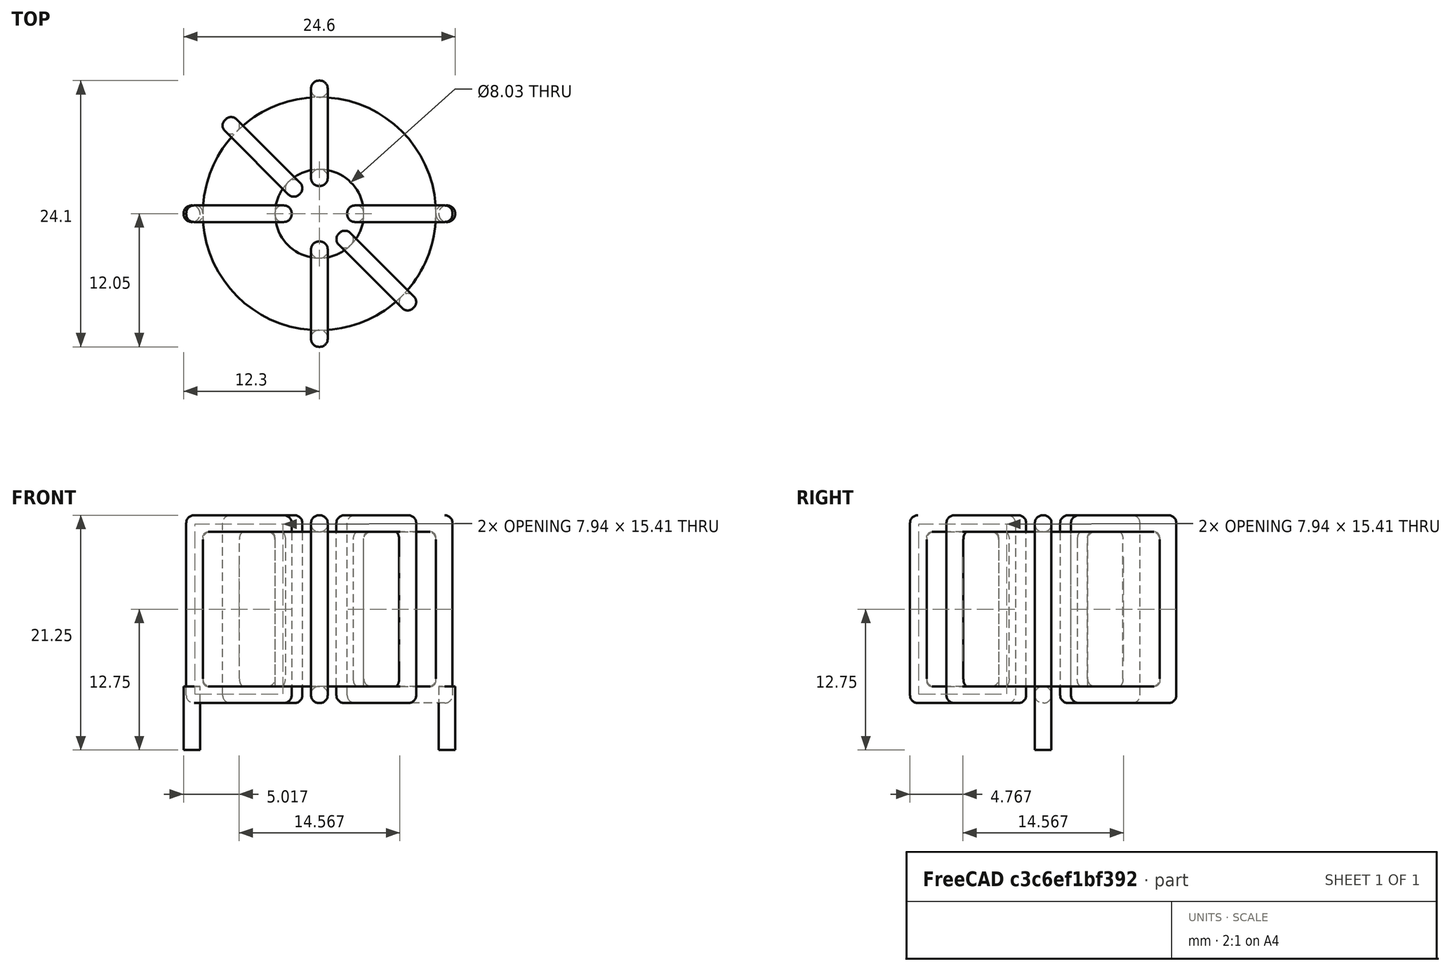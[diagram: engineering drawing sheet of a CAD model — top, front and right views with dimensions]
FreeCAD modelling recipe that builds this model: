
FCSTD DOCUMENT  (FreeCAD 0.16R6703 (Git))
Label: L_Toroid_Horizontal_D24.1mm_P23.10mm_Bourns_2200series
License: All rights reserved
LicenseURL: http://en.wikipedia.org/wiki/All_rights_reserved
objects: Sketcher::SketchObject×6, PartDesign::Pad×6, PartDesign::Fillet×5, Spreadsheet::Sheet×1
note: 23 computed .brp shape members not serialized (recipe doc carries the construction recipe); baked Part::Feature solids carry a one-line shape summary decoded from their .brp

FEATURE [Spreadsheet::Sheet] Spreadsheet  label="dimensions"
  cells = A1=Wx; B1(Wx)=24.1; C1(WW)=8.033333333333333; D1=24.1; A2=Wy; B2(Wy)=24.1; D2=24.1; A3=RM; B3(RMx)=23.1; C3(RMy)=0; A4=d_wire; B4(d_wire)=1.5; A5=H; B5(H)=14; A6=offsetx; B6(offsetx)=0.5
FEATURE [Sketcher::SketchObject] Sketch
  Placement = pos=(0,0,2) rot=(0,0,1;0rad)
  expr: Placement.Base.z = 0.5 + Spreadsheet.d_wire
  expr: Constraints[0] = Spreadsheet.Wx / 2 - Spreadsheet.d_wire
  expr: Constraints[4] = Spreadsheet.WW / 2
  expr: Constraints[2] = Spreadsheet.RMy / 2
  expr: Constraints[1] = Spreadsheet.RMx / 2
  sketch-geometry (2):
    g0: Circle CenterX=11.55 CenterY=0 CenterZ=0 NormalX=0 NormalY=0 NormalZ=1 Radius=10.55
    g1: Circle CenterX=11.55 CenterY=0 CenterZ=0 NormalX=0 NormalY=0 NormalZ=1 Radius=4.01667
  constraints (5):
    c: Radius(g0) = 10.55
    c: DistanceX(g-1,g0) = 11.55
    c: DistanceY(g-1,g0) = 0
    c: Coincident(g1,g0)
    c: Radius(g1) = 4.01667
FEATURE [PartDesign::Pad] Pad
  Length = 14
  Length2 = 100
  Placement = pos=(0,0,2) rot=(0,0,1;0rad)
  Sketch = -> Sketch
  Type = 0
  expr: Length = Spreadsheet.H
FEATURE [Sketcher::SketchObject] Sketch001
  Placement = pos=(0,0,1.25) rot=(0,0,1;0rad)
  expr: Placement.Base.z = 0.5 + Spreadsheet.d_wire * 0.5
  expr: Constraints[4] = Spreadsheet.RMx
  expr: Constraints[2] = Spreadsheet.RMy
  expr: Constraints[1] = Spreadsheet.d_wire / 2
  sketch-geometry (2):
    g0: Circle CenterX=0 CenterY=0 CenterZ=0 NormalX=0 NormalY=0 NormalZ=1 Radius=0.75
    g1: Circle CenterX=23.1 CenterY=0 CenterZ=0 NormalX=0 NormalY=0 NormalZ=1 Radius=0.75
  constraints (5):
    c: Equal(g0,g1)
    c: Radius(g0) = 0.75
    c: DistanceY(g-1,g1) = 0
    c: Coincident(g0,g-1)
    c: DistanceX(g-1,g1) = 23.1
FEATURE [PartDesign::Pad] Pad001
  Length = 0.75
  Length2 = 5
  Placement = pos=(0,0,1.25) rot=(0,0,1;0rad)
  Reversed = true
  Sketch = -> Sketch001
  Type = 4
  expr: Length2 = 3.5 + Spreadsheet.d_wire
  expr: Length = Spreadsheet.d_wire / 2
FEATURE [PartDesign::Fillet] Fillet
  Base = -> Pad [Edge6,Edge3,Edge2]
  Placement = pos=(0,0,2) rot=(0,0,1;0rad)
  Radius = 0.5
FEATURE [Sketcher::SketchObject] Sketch003
  Placement = pos=(11.55,0,0) rot=(1,0,0;1.5708rad)
  expr: Placement.Base.x = Spreadsheet.RMx / 2
  expr: Constraints[49] = Spreadsheet.Wx - Spreadsheet.d_wire * 2
  expr: Constraints[44] = Spreadsheet.d_wire
  expr: Constraints[23] = Spreadsheet.H
  expr: Constraints[22] = Spreadsheet.Wx / 2 - Spreadsheet.d_wire
  expr: Placement.Base.y = Spreadsheet.RMy / 2
  expr: Constraints[21] = (Spreadsheet.Wx - Spreadsheet.WW) / 2 - Spreadsheet.d_wire
  expr: Constraints[19] = Spreadsheet.d_wire
  expr: Constraints[17] = Spreadsheet.d_wire
  expr: Constraints[18] = Spreadsheet.d_wire
  expr: Constraints[16] = Spreadsheet.d_wire
  sketch-geometry (16):
    g0: LineSegment StartX=-2.51667 StartY=0.5 StartZ=0 EndX=-12.05 EndY=0.5 EndZ=0
    g1: LineSegment StartX=-12.05 StartY=0.5 StartZ=0 EndX=-12.05 EndY=17.5 EndZ=0
    g2: LineSegment StartX=-12.05 StartY=17.5 StartZ=0 EndX=-2.51667 EndY=17.5 EndZ=0
    g3: LineSegment StartX=-2.51667 StartY=17.5 StartZ=0 EndX=-2.51667 EndY=0.5 EndZ=0
    g4: LineSegment StartX=-10.55 StartY=16 StartZ=0 EndX=-4.01667 EndY=16 EndZ=0
    g5: LineSegment StartX=-4.01667 StartY=16 StartZ=0 EndX=-4.01667 EndY=2 EndZ=0
    g6: LineSegment StartX=-4.01667 StartY=2 StartZ=0 EndX=-10.55 EndY=2 EndZ=0
    g7: LineSegment StartX=-10.55 StartY=2 StartZ=0 EndX=-10.55 EndY=16 EndZ=0
    g8: LineSegment StartX=2.51667 StartY=17.5 StartZ=0 EndX=12.05 EndY=17.5 EndZ=0
    g9: LineSegment StartX=12.05 StartY=17.5 StartZ=0 EndX=12.05 EndY=0.5 EndZ=0
    g10: LineSegment StartX=12.05 StartY=0.5 StartZ=0 EndX=2.51667 EndY=0.5 EndZ=0
    g11: LineSegment StartX=2.51667 StartY=0.5 StartZ=0 EndX=2.51667 EndY=17.5 EndZ=0
    g12: LineSegment StartX=4.01667 StartY=16 StartZ=0 EndX=10.55 EndY=16 EndZ=0
    g13: LineSegment StartX=10.55 StartY=16 StartZ=0 EndX=10.55 EndY=2 EndZ=0
    g14: LineSegment StartX=10.55 StartY=2 StartZ=0 EndX=4.01667 EndY=2 EndZ=0
    g15: LineSegment StartX=4.01667 StartY=2 StartZ=0 EndX=4.01667 EndY=16 EndZ=0
  constraints (50):
    c: Horizontal(g0)
    c: Coincident(g1,g0)
    c: Vertical(g1)
    c: Coincident(g2,g1)
    c: Horizontal(g2)
    c: Coincident(g3,g2)
    c: Coincident(g3,g0)
    c: Vertical(g3)
    c: Coincident(g4,g5)
    c: Coincident(g5,g6)
    c: Coincident(g6,g7)
    c: Coincident(g7,g4)
    c: Horizontal(g4)
    c: Horizontal(g6)
    c: Vertical(g5)
    c: Vertical(g7)
    c: DistanceX(g1,g4) = 1.5
    c: DistanceY(g4,g1) = 1.5
    c: DistanceX(g5,g0) = 1.5
    c: DistanceY(g0,g5) = 1.5
    c: DistanceY(g-1,g0) = 0.5
    c: DistanceX(g6,g6) = 6.53333
    c: DistanceX(g6,g-1) = 10.55
    c: DistanceY(g7,g7) = 14
    c: Coincident(g8,g9)
    c: Coincident(g9,g10)
    c: Coincident(g10,g11)
    c: Coincident(g11,g8)
    c: Horizontal(g8)
    c: Horizontal(g10)
    c: Vertical(g9)
    c: Vertical(g11)
    c: Coincident(g12,g13)
    c: Coincident(g13,g14)
    c: Coincident(g14,g15)
    c: Coincident(g15,g12)
    c: Horizontal(g12)
    c: Horizontal(g14)
    c: Vertical(g13)
    c: Vertical(g15)
    c: DistanceY(g8,g2) = 0
    c: DistanceY(g10,g0) = 0
    c: DistanceY(g14,g5) = 0
    c: DistanceY(g12,g4) = 0
    c: DistanceX(g8,g12) = 1.5
    c: Equal(g8,g2)
    c: Equal(g12,g4)
    c: Equal(g9,g1)
    c: Equal(g13,g7)
    c: DistanceX(g4,g12) = 21.1
FEATURE [PartDesign::Pad] Pad002
  Length = 1.5
  Length2 = 100
  Midplane = true
  Placement = pos=(11.55,0,0) rot=(1,0,0;1.5708rad)
  Sketch = -> Sketch003
  Type = 0
  expr: Length = Spreadsheet.d_wire
FEATURE [PartDesign::Fillet] Fillet001
  Base = -> Pad002 [Edge38,Edge41,Edge42,Edge43,Edge29,Edge32,Edge33,Edge34,Edge25,Edge35,Edge36,Edge13,Edge14,Edge15,Edge16,Edge17,Edge18,Edge19,Edge1,Edge2,Edge3,Edge4,Edge5,Edge6,Edge7,Edge37,Edge39,Edge40,Edge20,Edge23,Edge24,Edge21,Edge22,Edge8,Edge9,Edge10,Edge11,Edge12,Edge26,Edge27,+8 more]
  Placement = pos=(11.55,0,0) rot=(1,0,0;1.5708rad)
  Radius = 0.705
  expr: Radius = Spreadsheet.d_wire * 0.47
FEATURE [Sketcher::SketchObject] Sketch004
  Placement = pos=(11.55,0,0) rot=(0.862856,0.357407,0.357407;1.71777rad)
  expr: Placement.Base.x = Spreadsheet.RMx / 2
  expr: Constraints[49] = Spreadsheet.Wx - 2 * Spreadsheet.d_wire
  expr: Constraints[44] = Spreadsheet.d_wire
  expr: Constraints[23] = Spreadsheet.H
  expr: Constraints[22] = Spreadsheet.Wx / 2 - Spreadsheet.d_wire
  expr: Placement.Base.y = Spreadsheet.RMy / 2
  expr: Constraints[21] = (Spreadsheet.Wx - Spreadsheet.WW) / 2 - Spreadsheet.d_wire
  expr: Constraints[19] = Spreadsheet.d_wire
  expr: Constraints[17] = Spreadsheet.d_wire
  expr: Constraints[18] = Spreadsheet.d_wire
  expr: Constraints[16] = Spreadsheet.d_wire
  sketch-geometry (16):
    g0: LineSegment StartX=-2.51667 StartY=0.5 StartZ=0 EndX=-12.05 EndY=0.5 EndZ=0
    g1: LineSegment StartX=-12.05 StartY=0.5 StartZ=0 EndX=-12.05 EndY=17.5 EndZ=0
    g2: LineSegment StartX=-12.05 StartY=17.5 StartZ=0 EndX=-2.51667 EndY=17.5 EndZ=0
    g3: LineSegment StartX=-2.51667 StartY=17.5 StartZ=0 EndX=-2.51667 EndY=0.5 EndZ=0
    g4: LineSegment StartX=-10.55 StartY=16 StartZ=0 EndX=-4.01667 EndY=16 EndZ=0
    g5: LineSegment StartX=-4.01667 StartY=16 StartZ=0 EndX=-4.01667 EndY=2 EndZ=0
    g6: LineSegment StartX=-4.01667 StartY=2 StartZ=0 EndX=-10.55 EndY=2 EndZ=0
    g7: LineSegment StartX=-10.55 StartY=2 StartZ=0 EndX=-10.55 EndY=16 EndZ=0
    g8: LineSegment StartX=2.51667 StartY=17.5 StartZ=0 EndX=12.05 EndY=17.5 EndZ=0
    g9: LineSegment StartX=12.05 StartY=17.5 StartZ=0 EndX=12.05 EndY=0.5 EndZ=0
    g10: LineSegment StartX=12.05 StartY=0.5 StartZ=0 EndX=2.51667 EndY=0.5 EndZ=0
    g11: LineSegment StartX=2.51667 StartY=0.5 StartZ=0 EndX=2.51667 EndY=17.5 EndZ=0
    g12: LineSegment StartX=4.01667 StartY=16 StartZ=0 EndX=10.55 EndY=16 EndZ=0
    g13: LineSegment StartX=10.55 StartY=16 StartZ=0 EndX=10.55 EndY=2 EndZ=0
    g14: LineSegment StartX=10.55 StartY=2 StartZ=0 EndX=4.01667 EndY=2 EndZ=0
    g15: LineSegment StartX=4.01667 StartY=2 StartZ=0 EndX=4.01667 EndY=16 EndZ=0
  constraints (50):
    c: Horizontal(g0)
    c: Coincident(g1,g0)
    c: Vertical(g1)
    c: Coincident(g2,g1)
    c: Horizontal(g2)
    c: Coincident(g3,g2)
    c: Coincident(g3,g0)
    c: Vertical(g3)
    c: Coincident(g4,g5)
    c: Coincident(g5,g6)
    c: Coincident(g6,g7)
    c: Coincident(g7,g4)
    c: Horizontal(g4)
    c: Horizontal(g6)
    c: Vertical(g5)
    c: Vertical(g7)
    c: DistanceX(g1,g4) = 1.5
    c: DistanceY(g4,g1) = 1.5
    c: DistanceX(g5,g0) = 1.5
    c: DistanceY(g0,g5) = 1.5
    c: DistanceY(g-1,g0) = 0.5
    c: DistanceX(g6,g6) = 6.53333
    c: DistanceX(g6,g-1) = 10.55
    c: DistanceY(g7,g7) = 14
    c: Coincident(g8,g9)
    c: Coincident(g9,g10)
    c: Coincident(g10,g11)
    c: Coincident(g11,g8)
    c: Horizontal(g8)
    c: Horizontal(g10)
    c: Vertical(g9)
    c: Vertical(g11)
    c: Coincident(g12,g13)
    c: Coincident(g13,g14)
    c: Coincident(g14,g15)
    c: Coincident(g15,g12)
    c: Horizontal(g12)
    c: Horizontal(g14)
    c: Vertical(g13)
    c: Vertical(g15)
    c: DistanceY(g8,g2) = 0
    c: DistanceY(g10,g0) = 0
    c: DistanceY(g14,g5) = 0
    c: DistanceY(g12,g4) = 0
    c: DistanceX(g8,g12) = 1.5
    c: Equal(g8,g2)
    c: Equal(g12,g4)
    c: Equal(g9,g1)
    c: Equal(g13,g7)
    c: DistanceX(g4,g12) = 21.1
FEATURE [PartDesign::Pad] Pad003
  Length = 1.5
  Length2 = 100
  Midplane = true
  Placement = pos=(11.55,0,0) rot=(0.862856,0.357407,0.357407;1.71777rad)
  Sketch = -> Sketch004
  Type = 0
  expr: Length = Spreadsheet.d_wire
FEATURE [PartDesign::Fillet] Fillet002
  Base = -> Pad003 [Edge38,Edge41,Edge42,Edge43,Edge29,Edge32,Edge33,Edge34,Edge25,Edge35,Edge36,Edge13,Edge14,Edge15,Edge16,Edge17,Edge18,Edge19,Edge1,Edge2,Edge3,Edge4,Edge5,Edge6,Edge7,Edge37,Edge39,Edge40,Edge20,Edge23,Edge24,Edge21,Edge22,Edge8,Edge9,Edge10,Edge11,Edge12,Edge26,Edge27,+8 more]
  Placement = pos=(11.55,0,0) rot=(0.862856,0.357407,0.357407;1.71777rad)
  Radius = 0.705
  expr: Radius = Spreadsheet.d_wire * 0.47
FEATURE [Sketcher::SketchObject] Sketch005
  Placement = pos=(11.55,0,0) rot=(0.862856,-0.357407,-0.357407;1.71777rad)
  expr: Placement.Base.x = Spreadsheet.RMx / 2
  expr: Constraints[49] = Spreadsheet.Wx - 2 * Spreadsheet.d_wire
  expr: Constraints[44] = Spreadsheet.d_wire
  expr: Constraints[23] = Spreadsheet.H
  expr: Constraints[22] = Spreadsheet.Wx / 2 - Spreadsheet.d_wire
  expr: Placement.Base.y = Spreadsheet.RMy / 2
  expr: Constraints[21] = (Spreadsheet.Wx - Spreadsheet.WW) / 2 - Spreadsheet.d_wire
  expr: Constraints[19] = Spreadsheet.d_wire
  expr: Constraints[17] = Spreadsheet.d_wire
  expr: Constraints[18] = Spreadsheet.d_wire
  expr: Constraints[16] = Spreadsheet.d_wire
  sketch-geometry (16):
    g0: LineSegment StartX=-2.51667 StartY=0.5 StartZ=0 EndX=-12.05 EndY=0.5 EndZ=0
    g1: LineSegment StartX=-12.05 StartY=0.5 StartZ=0 EndX=-12.05 EndY=17.5 EndZ=0
    g2: LineSegment StartX=-12.05 StartY=17.5 StartZ=0 EndX=-2.51667 EndY=17.5 EndZ=0
    g3: LineSegment StartX=-2.51667 StartY=17.5 StartZ=0 EndX=-2.51667 EndY=0.5 EndZ=0
    g4: LineSegment StartX=-10.55 StartY=16 StartZ=0 EndX=-4.01667 EndY=16 EndZ=0
    g5: LineSegment StartX=-4.01667 StartY=16 StartZ=0 EndX=-4.01667 EndY=2 EndZ=0
    g6: LineSegment StartX=-4.01667 StartY=2 StartZ=0 EndX=-10.55 EndY=2 EndZ=0
    g7: LineSegment StartX=-10.55 StartY=2 StartZ=0 EndX=-10.55 EndY=16 EndZ=0
    g8: LineSegment StartX=2.51667 StartY=17.5 StartZ=0 EndX=12.05 EndY=17.5 EndZ=0
    g9: LineSegment StartX=12.05 StartY=17.5 StartZ=0 EndX=12.05 EndY=0.5 EndZ=0
    g10: LineSegment StartX=12.05 StartY=0.5 StartZ=0 EndX=2.51667 EndY=0.5 EndZ=0
    g11: LineSegment StartX=2.51667 StartY=0.5 StartZ=0 EndX=2.51667 EndY=17.5 EndZ=0
    g12: LineSegment StartX=4.01667 StartY=16 StartZ=0 EndX=10.55 EndY=16 EndZ=0
    g13: LineSegment StartX=10.55 StartY=16 StartZ=0 EndX=10.55 EndY=2 EndZ=0
    g14: LineSegment StartX=10.55 StartY=2 StartZ=0 EndX=4.01667 EndY=2 EndZ=0
    g15: LineSegment StartX=4.01667 StartY=2 StartZ=0 EndX=4.01667 EndY=16 EndZ=0
  constraints (50):
    c: Horizontal(g0)
    c: Coincident(g1,g0)
    c: Vertical(g1)
    c: Coincident(g2,g1)
    c: Horizontal(g2)
    c: Coincident(g3,g2)
    c: Coincident(g3,g0)
    c: Vertical(g3)
    c: Coincident(g4,g5)
    c: Coincident(g5,g6)
    c: Coincident(g6,g7)
    c: Coincident(g7,g4)
    c: Horizontal(g4)
    c: Horizontal(g6)
    c: Vertical(g5)
    c: Vertical(g7)
    c: DistanceX(g1,g4) = 1.5
    c: DistanceY(g4,g1) = 1.5
    c: DistanceX(g5,g0) = 1.5
    c: DistanceY(g0,g5) = 1.5
    c: DistanceY(g-1,g0) = 0.5
    c: DistanceX(g6,g6) = 6.53333
    c: DistanceX(g6,g-1) = 10.55
    c: DistanceY(g7,g7) = 14
    c: Coincident(g8,g9)
    c: Coincident(g9,g10)
    c: Coincident(g10,g11)
    c: Coincident(g11,g8)
    c: Horizontal(g8)
    c: Horizontal(g10)
    c: Vertical(g9)
    c: Vertical(g11)
    c: Coincident(g12,g13)
    c: Coincident(g13,g14)
    c: Coincident(g14,g15)
    c: Coincident(g15,g12)
    c: Horizontal(g12)
    c: Horizontal(g14)
    c: Vertical(g13)
    c: Vertical(g15)
    c: DistanceY(g8,g2) = 0
    c: DistanceY(g10,g0) = 0
    c: DistanceY(g14,g5) = 0
    c: DistanceY(g12,g4) = 0
    c: DistanceX(g8,g12) = 1.5
    c: Equal(g8,g2)
    c: Equal(g12,g4)
    c: Equal(g9,g1)
    c: Equal(g13,g7)
    c: DistanceX(g4,g12) = 21.1
FEATURE [PartDesign::Pad] Pad004
  Length = 1.5
  Length2 = 100
  Midplane = true
  Placement = pos=(11.55,0,0) rot=(0.862856,-0.357407,-0.357407;1.71777rad)
  Sketch = -> Sketch005
  Type = 0
  expr: Length = Spreadsheet.d_wire
FEATURE [PartDesign::Fillet] Fillet003
  Base = -> Pad004 [Edge38,Edge41,Edge42,Edge43,Edge29,Edge32,Edge33,Edge34,Edge25,Edge35,Edge36,Edge13,Edge14,Edge15,Edge16,Edge17,Edge18,Edge19,Edge1,Edge2,Edge3,Edge4,Edge5,Edge6,Edge7,Edge37,Edge39,Edge40,Edge20,Edge23,Edge24,Edge21,Edge22,Edge8,Edge9,Edge10,Edge11,Edge12,Edge26,Edge27,+8 more]
  Placement = pos=(11.55,0,0) rot=(0.862856,-0.357407,-0.357407;1.71777rad)
  Radius = 0.705
  expr: Radius = Spreadsheet.d_wire * 0.47
FEATURE [Sketcher::SketchObject] Sketch006
  Placement = pos=(11.55,0,0) rot=(0.57735,0.57735,0.57735;2.0944rad)
  expr: Placement.Base.x = Spreadsheet.RMx / 2
  expr: Constraints[49] = Spreadsheet.Wx - Spreadsheet.d_wire * 2
  expr: Constraints[44] = Spreadsheet.d_wire
  expr: Constraints[23] = Spreadsheet.H
  expr: Constraints[22] = Spreadsheet.Wx / 2 - Spreadsheet.d_wire
  expr: Placement.Base.y = Spreadsheet.RMy / 2
  expr: Constraints[21] = (Spreadsheet.Wx - Spreadsheet.WW) / 2 - Spreadsheet.d_wire
  expr: Constraints[19] = Spreadsheet.d_wire
  expr: Constraints[17] = Spreadsheet.d_wire
  expr: Constraints[18] = Spreadsheet.d_wire
  expr: Constraints[16] = Spreadsheet.d_wire
  sketch-geometry (16):
    g0: LineSegment StartX=-2.51667 StartY=0.5 StartZ=0 EndX=-12.05 EndY=0.5 EndZ=0
    g1: LineSegment StartX=-12.05 StartY=0.5 StartZ=0 EndX=-12.05 EndY=17.5 EndZ=0
    g2: LineSegment StartX=-12.05 StartY=17.5 StartZ=0 EndX=-2.51667 EndY=17.5 EndZ=0
    g3: LineSegment StartX=-2.51667 StartY=17.5 StartZ=0 EndX=-2.51667 EndY=0.5 EndZ=0
    g4: LineSegment StartX=-10.55 StartY=16 StartZ=0 EndX=-4.01667 EndY=16 EndZ=0
    g5: LineSegment StartX=-4.01667 StartY=16 StartZ=0 EndX=-4.01667 EndY=2 EndZ=0
    g6: LineSegment StartX=-4.01667 StartY=2 StartZ=0 EndX=-10.55 EndY=2 EndZ=0
    g7: LineSegment StartX=-10.55 StartY=2 StartZ=0 EndX=-10.55 EndY=16 EndZ=0
    g8: LineSegment StartX=2.51667 StartY=17.5 StartZ=0 EndX=12.05 EndY=17.5 EndZ=0
    g9: LineSegment StartX=12.05 StartY=17.5 StartZ=0 EndX=12.05 EndY=0.5 EndZ=0
    g10: LineSegment StartX=12.05 StartY=0.5 StartZ=0 EndX=2.51667 EndY=0.5 EndZ=0
    g11: LineSegment StartX=2.51667 StartY=0.5 StartZ=0 EndX=2.51667 EndY=17.5 EndZ=0
    g12: LineSegment StartX=4.01667 StartY=16 StartZ=0 EndX=10.55 EndY=16 EndZ=0
    g13: LineSegment StartX=10.55 StartY=16 StartZ=0 EndX=10.55 EndY=2 EndZ=0
    g14: LineSegment StartX=10.55 StartY=2 StartZ=0 EndX=4.01667 EndY=2 EndZ=0
    g15: LineSegment StartX=4.01667 StartY=2 StartZ=0 EndX=4.01667 EndY=16 EndZ=0
  constraints (50):
    c: Horizontal(g0)
    c: Coincident(g1,g0)
    c: Vertical(g1)
    c: Coincident(g2,g1)
    c: Horizontal(g2)
    c: Coincident(g3,g2)
    c: Coincident(g3,g0)
    c: Vertical(g3)
    c: Coincident(g4,g5)
    c: Coincident(g5,g6)
    c: Coincident(g6,g7)
    c: Coincident(g7,g4)
    c: Horizontal(g4)
    c: Horizontal(g6)
    c: Vertical(g5)
    c: Vertical(g7)
    c: DistanceX(g1,g4) = 1.5
    c: DistanceY(g4,g1) = 1.5
    c: DistanceX(g5,g0) = 1.5
    c: DistanceY(g0,g5) = 1.5
    c: DistanceY(g-1,g0) = 0.5
    c: DistanceX(g6,g6) = 6.53333
    c: DistanceX(g6,g-1) = 10.55
    c: DistanceY(g7,g7) = 14
    c: Coincident(g8,g9)
    c: Coincident(g9,g10)
    c: Coincident(g10,g11)
    c: Coincident(g11,g8)
    c: Horizontal(g8)
    c: Horizontal(g10)
    c: Vertical(g9)
    c: Vertical(g11)
    c: Coincident(g12,g13)
    c: Coincident(g13,g14)
    c: Coincident(g14,g15)
    c: Coincident(g15,g12)
    c: Horizontal(g12)
    c: Horizontal(g14)
    c: Vertical(g13)
    c: Vertical(g15)
    c: DistanceY(g8,g2) = 0
    c: DistanceY(g10,g0) = 0
    c: DistanceY(g14,g5) = 0
    c: DistanceY(g12,g4) = 0
    c: DistanceX(g8,g12) = 1.5
    c: Equal(g8,g2)
    c: Equal(g12,g4)
    c: Equal(g9,g1)
    c: Equal(g13,g7)
    c: DistanceX(g4,g12) = 21.1
FEATURE [PartDesign::Pad] Pad005
  Length = 1.5
  Length2 = 100
  Midplane = true
  Placement = pos=(11.55,0,0) rot=(0.57735,0.57735,0.57735;2.0944rad)
  Sketch = -> Sketch006
  Type = 0
  expr: Length = Spreadsheet.d_wire
FEATURE [PartDesign::Fillet] Fillet004
  Base = -> Pad005 [Edge38,Edge41,Edge42,Edge43,Edge29,Edge32,Edge33,Edge34,Edge25,Edge35,Edge36,Edge13,Edge14,Edge15,Edge16,Edge17,Edge18,Edge19,Edge1,Edge2,Edge3,Edge4,Edge5,Edge6,Edge7,Edge37,Edge39,Edge40,Edge20,Edge23,Edge24,Edge21,Edge22,Edge8,Edge9,Edge10,Edge11,Edge12,Edge26,Edge27,+8 more]
  Placement = pos=(11.55,0,0) rot=(0.57735,0.57735,0.57735;2.0944rad)
  Radius = 0.705
  expr: Radius = Spreadsheet.d_wire * 0.47
